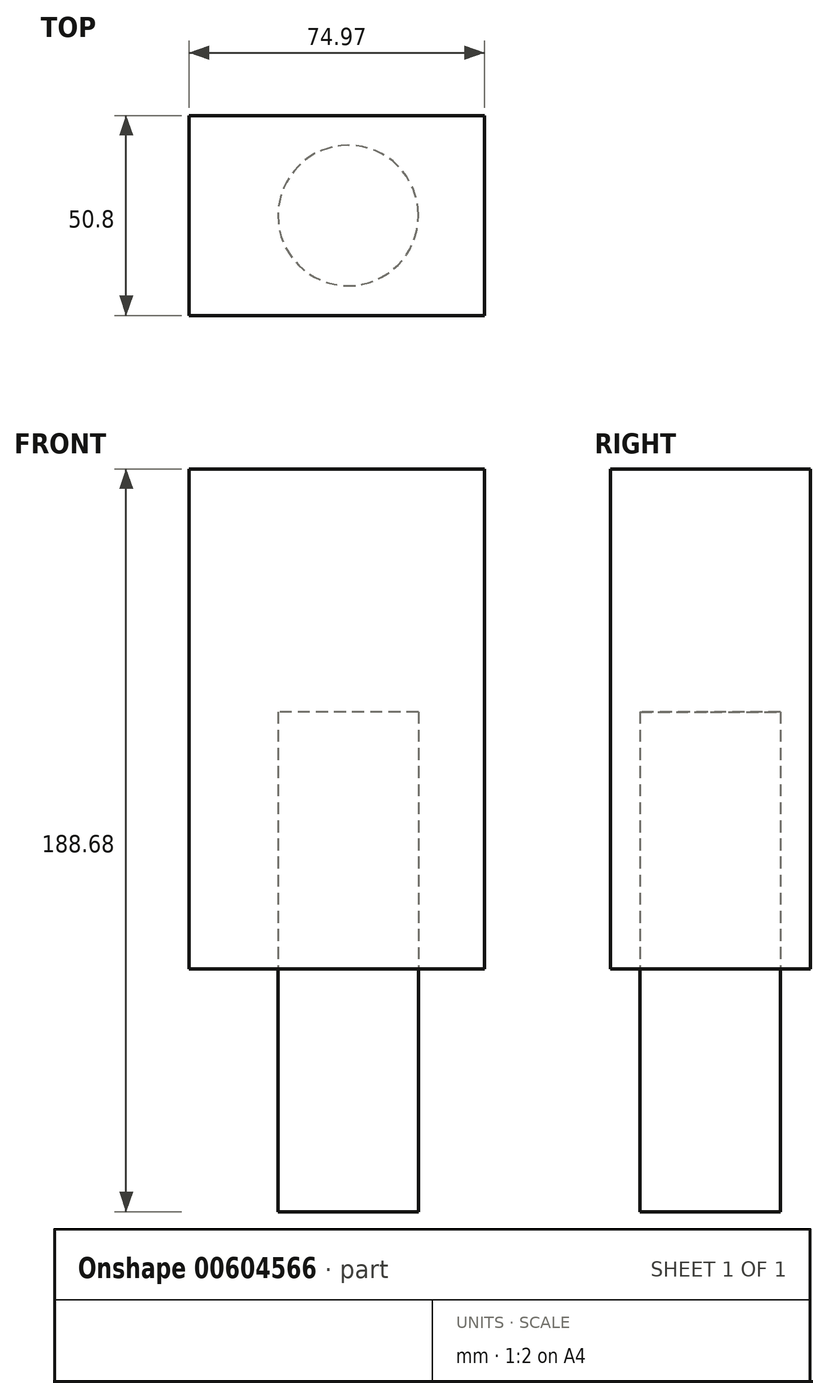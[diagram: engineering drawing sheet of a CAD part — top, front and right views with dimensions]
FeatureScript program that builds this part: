
annotation { "Feature Type Name" : "Feature", "Feature Type Description" : "" }
export const myFeature = defineFeature(function(context is Context, id is Id, definition is map)
    precondition{}
    {
        {
            var Q0;
            Q0=qCreatedBy(makeId("Front.planeOp"),FACE);
            var sketch = newSketch(context, id + "F0", { "sketchPlane" : qUnion([Q0])});
            skLineSegment(sketch, "E0.bottom", {"start": v(-40.4, -13.18) * mm, "end": v(34.58, -13.18) * mm});
            skLineSegment(sketch, "E0.top", {"start": v(-40.4, 61.68) * mm, "end": v(34.58, 61.68) * mm});
            skLineSegment(sketch, "E0.left", {"start": v(-40.4, -13.18) * mm, "end": v(-40.4, 61.68) * mm});
            skLineSegment(sketch, "E0.right", {"start": v(34.58, -13.18) * mm, "end": v(34.58, 61.68) * mm});
            skLineSegment(sketch, "E1.bottom", {"start": v(92.8, -59.16) * mm, "end": v(-40.4, -59.16) * mm});
            skLineSegment(sketch, "E1.top", {"start": v(92.8, -13.18) * mm, "end": v(-40.4, -13.18) * mm});
            skLineSegment(sketch, "E1.left", {"start": v(92.8, -59.16) * mm, "end": v(92.8, -13.18) * mm});
            skLineSegment(sketch, "E1.right", {"start": v(-40.4, -59.16) * mm, "end": v(-40.4, -13.18) * mm});
            skLineSegment(sketch, "E2.bottom", {"start": v(35.3, 60.91) * mm, "end": v(-71.67, 60.91) * mm});
            skLineSegment(sketch, "E2.top", {"start": v(35.3, -59.16) * mm, "end": v(-71.67, -59.16) * mm});
            skLineSegment(sketch, "E2.left", {"start": v(35.3, 60.91) * mm, "end": v(35.3, -59.16) * mm});
            skLineSegment(sketch, "E2.right", {"start": v(-71.67, 60.91) * mm, "end": v(-71.67, -59.16) * mm});
            skSolve(sketch);
        }
        {
            var Q0;
            Q0=sQuery(id+"F0.wireOp",EDGE,"E0.top");
            extrude(context, id + "F1", {"bodyType" : ToolBodyType.SURFACE, "surfaceEntities" : qUnion([Q0]), "depth" : 25.4 * mm, "offsetDistance" : 25.4 * mm, "hasSecondDirection" : true, "secondDirectionOppositeDirection" : true, "secondDirectionDepth" : 25.4 * mm});
        }
        {
            var Q0;
            Q0=qCreatedBy(makeId("Top.planeOp"),FACE);
            var sketch = newSketch(context, id + "F2", { "sketchPlane" : qUnion([Q0])});
            skCircle(sketch, "E3", {"center": v(0, 0) * mm, "radius": 17.83 * mm});
            skSolve(sketch);
        }
        {
            var Q0;
            Q0=makeQuery(id+"F2.imprint","IMPRINT",FACE,{"disambiguationData":[TD([[makeQuery(id+"F2.imprint","IMPRINT",EDGE,{"derivedFrom":sQuery(id+"F2.wireOp",EDGE,"E3")}),1.0]])]});
            var Q1;
            Q1=makeQuery(id+"F1.opExtrude","SWEPT_FACE",FACE,{"disambiguationData":[OSD([sQuery(id+"F0.wireOp",EDGE,"E0.top")])]});
            extrude(context, id + "F3", {"entities" : qUnion([Q0, Q1]), "depth" : 127 * mm, "offsetDistance" : 25.4 * mm});
        }
    });
